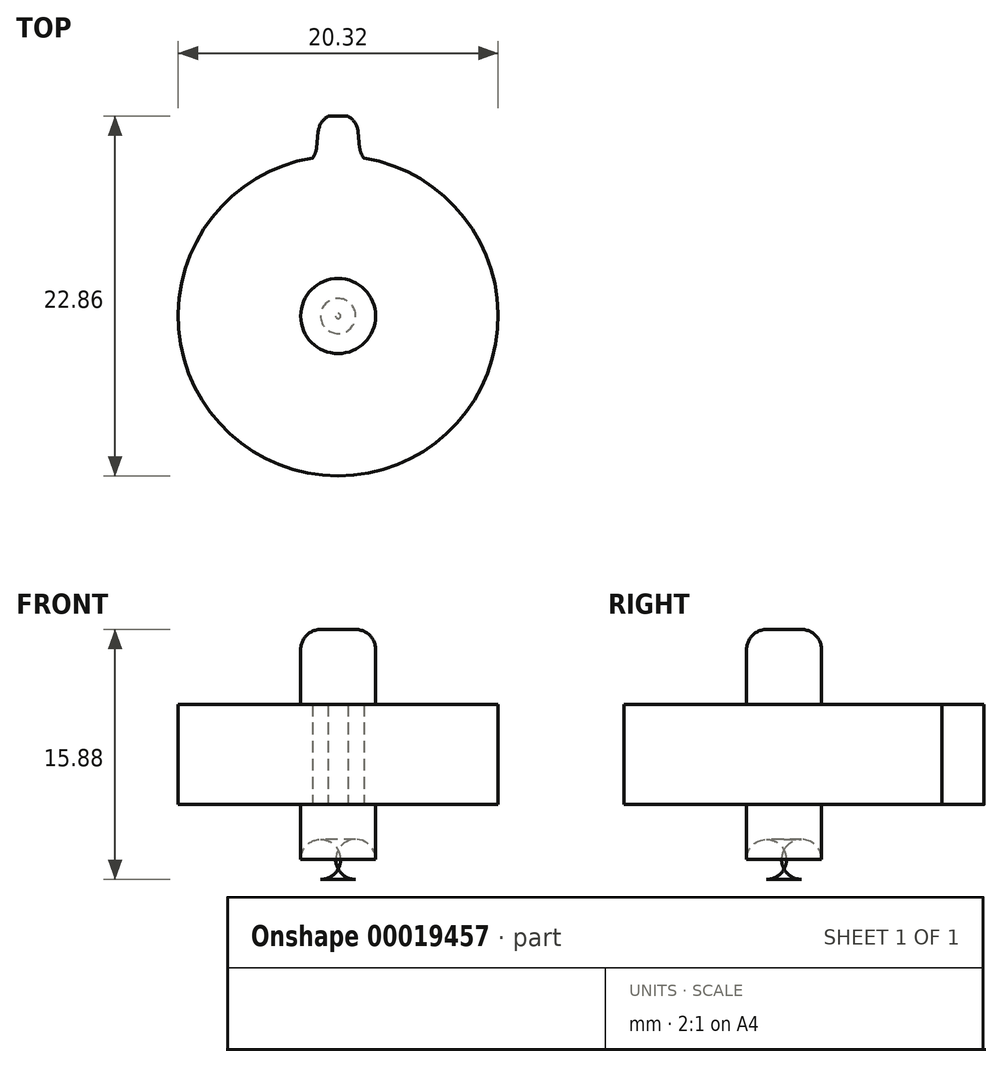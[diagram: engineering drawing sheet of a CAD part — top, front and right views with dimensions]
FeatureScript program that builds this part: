
annotation { "Feature Type Name" : "Feature", "Feature Type Description" : "" }
export const myFeature = defineFeature(function(context is Context, id is Id, definition is map)
    precondition{}
    {
        {
            var Q0;
            Q0=qCreatedBy(makeId("Top.planeOp"),FACE);
            var sketch = newSketch(context, id + "F0", { "sketchPlane" : qUnion([Q0])});
            skArc(sketch, "E0", {"start": v(0.64, 12.68) * mm, "mid": v(0, 12.7) * mm, "end": v(-0.64, 12.68) * mm});
            skLineSegment(sketch, "E1", {"start": v(1.26, 11.72) * mm, "end": v(1.37, 10.68) * mm});
            skCircle(sketch, "E2", {"center": v(0, 0) * mm, "radius": 10.16 * mm});
            skArc(sketch, "E3", {"start": v(1.26, 11.72) * mm, "mid": v(1.07, 12.28) * mm, "end": v(0.64, 12.68) * mm});
            skArc(sketch, "E4", {"start": v(1.37, 10.68) * mm, "mid": v(1.46, 10.33) * mm, "end": v(1.64, 10.03) * mm});
            skLineSegment(sketch, "E5", {"start": v(3.66, 0) * mm, "end": v(0, 0) * mm, "construction": true});
            skLineSegment(sketch, "E6", {"start": v(0, 0) * mm, "end": v(0, 13.54) * mm, "construction": true});
            skLineSegment(sketch, "E7.MirrorCS", {"start": v(-1.26, 11.72) * mm, "end": v(-1.37, 10.68) * mm});
            skArc(sketch, "E8.MirrorCS", {"start": v(-1.26, 11.72) * mm, "mid": v(-1.07, 12.28) * mm, "end": v(-0.64, 12.68) * mm});
            skArc(sketch, "E9.MirrorCS", {"start": v(-1.37, 10.68) * mm, "mid": v(-1.46, 10.33) * mm, "end": v(-1.64, 10.03) * mm});
            skArc(sketch, "E10.1.0", {"start": v(-6.22, 10) * mm, "mid": v(-6.29, 10.6) * mm, "end": v(-6.08, 11.15) * mm});
            skArc(sketch, "E10.1.1", {"start": v(-4.93, 11.7) * mm, "mid": v(-5.51, 11.44) * mm, "end": v(-6.08, 11.15) * mm});
            skArc(sketch, "E10.1.2", {"start": v(-3.95, 11.1) * mm, "mid": v(-4.37, 11.52) * mm, "end": v(-4.93, 11.7) * mm});
            skArc(sketch, "E10.1.3", {"start": v(-5.87, 9.03) * mm, "mid": v(-5.8, 8.68) * mm, "end": v(-5.83, 8.32) * mm});
            skArc(sketch, "E10.1.4", {"start": v(-3.4, 10.22) * mm, "mid": v(-3.17, 9.94) * mm, "end": v(-2.88, 9.74) * mm});
            skLineSegment(sketch, "E10.1.5", {"start": v(-6.22, 10) * mm, "end": v(-5.87, 9.03) * mm});
            skLineSegment(sketch, "E10.1.6", {"start": v(-3.95, 11.1) * mm, "end": v(-3.4, 10.22) * mm});
            skArc(sketch, "E10.2.0", {"start": v(-9.95, 6.32) * mm, "mid": v(-10.26, 6.82) * mm, "end": v(-10.31, 7.41) * mm});
            skArc(sketch, "E10.2.1", {"start": v(-9.52, 8.4) * mm, "mid": v(-9.93, 7.92) * mm, "end": v(-10.31, 7.41) * mm});
            skArc(sketch, "E10.2.2", {"start": v(-8.37, 8.3) * mm, "mid": v(-8.93, 8.49) * mm, "end": v(-9.52, 8.4) * mm});
            skArc(sketch, "E10.2.3", {"start": v(-9.2, 5.59) * mm, "mid": v(-8.99, 5.3) * mm, "end": v(-8.86, 4.97) * mm});
            skArc(sketch, "E10.2.4", {"start": v(-7.5, 7.73) * mm, "mid": v(-7.17, 7.58) * mm, "end": v(-6.82, 7.53) * mm});
            skLineSegment(sketch, "E10.2.5", {"start": v(-9.95, 6.32) * mm, "end": v(-9.2, 5.59) * mm});
            skLineSegment(sketch, "E10.2.6", {"start": v(-8.37, 8.3) * mm, "end": v(-7.5, 7.73) * mm});
            skArc(sketch, "E10.3.0", {"start": v(-11.7, 1.38) * mm, "mid": v(-12.2, 1.7) * mm, "end": v(-12.5, 2.2) * mm});
            skArc(sketch, "E10.3.1", {"start": v(-12.22, 3.44) * mm, "mid": v(-12.38, 2.83) * mm, "end": v(-12.5, 2.2) * mm});
            skArc(sketch, "E10.3.2", {"start": v(-11.14, 3.84) * mm, "mid": v(-11.73, 3.77) * mm, "end": v(-12.22, 3.44) * mm});
            skArc(sketch, "E10.3.3", {"start": v(-10.72, 1.04) * mm, "mid": v(-10.4, 0.88) * mm, "end": v(-10.14, 0.64) * mm});
            skArc(sketch, "E10.3.4", {"start": v(-10.1, 3.71) * mm, "mid": v(-9.75, 3.72) * mm, "end": v(-9.41, 3.83) * mm});
            skLineSegment(sketch, "E10.3.5", {"start": v(-11.7, 1.38) * mm, "end": v(-10.72, 1.04) * mm});
            skLineSegment(sketch, "E10.3.6", {"start": v(-11.14, 3.84) * mm, "end": v(-10.1, 3.71) * mm});
            skArc(sketch, "E10.4.0", {"start": v(-11.14, -3.84) * mm, "mid": v(-11.73, -3.77) * mm, "end": v(-12.22, -3.44) * mm});
            skArc(sketch, "E10.4.1", {"start": v(-12.5, -2.2) * mm, "mid": v(-12.38, -2.83) * mm, "end": v(-12.22, -3.44) * mm});
            skArc(sketch, "E10.4.2", {"start": v(-11.7, -1.38) * mm, "mid": v(-12.2, -1.7) * mm, "end": v(-12.5, -2.2) * mm});
            skArc(sketch, "E10.4.3", {"start": v(-10.1, -3.71) * mm, "mid": v(-9.75, -3.72) * mm, "end": v(-9.41, -3.83) * mm});
            skArc(sketch, "E10.4.4", {"start": v(-10.72, -1.04) * mm, "mid": v(-10.4, -0.88) * mm, "end": v(-10.14, -0.64) * mm});
            skLineSegment(sketch, "E10.4.5", {"start": v(-11.14, -3.84) * mm, "end": v(-10.1, -3.71) * mm});
            skLineSegment(sketch, "E10.4.6", {"start": v(-11.7, -1.38) * mm, "end": v(-10.72, -1.04) * mm});
            skArc(sketch, "E10.5.0", {"start": v(-8.37, -8.3) * mm, "mid": v(-8.93, -8.49) * mm, "end": v(-9.52, -8.4) * mm});
            skArc(sketch, "E10.5.1", {"start": v(-10.31, -7.41) * mm, "mid": v(-9.93, -7.92) * mm, "end": v(-9.52, -8.4) * mm});
            skArc(sketch, "E10.5.2", {"start": v(-9.95, -6.32) * mm, "mid": v(-10.26, -6.82) * mm, "end": v(-10.31, -7.41) * mm});
            skArc(sketch, "E10.5.3", {"start": v(-7.5, -7.73) * mm, "mid": v(-7.17, -7.58) * mm, "end": v(-6.82, -7.53) * mm});
            skArc(sketch, "E10.5.4", {"start": v(-9.2, -5.59) * mm, "mid": v(-8.99, -5.3) * mm, "end": v(-8.86, -4.97) * mm});
            skLineSegment(sketch, "E10.5.5", {"start": v(-8.37, -8.3) * mm, "end": v(-7.5, -7.73) * mm});
            skLineSegment(sketch, "E10.5.6", {"start": v(-9.95, -6.32) * mm, "end": v(-9.2, -5.59) * mm});
            skArc(sketch, "E10.6.0", {"start": v(-3.95, -11.1) * mm, "mid": v(-4.37, -11.52) * mm, "end": v(-4.93, -11.7) * mm});
            skArc(sketch, "E10.6.1", {"start": v(-6.08, -11.15) * mm, "mid": v(-5.51, -11.44) * mm, "end": v(-4.93, -11.7) * mm});
            skArc(sketch, "E10.6.2", {"start": v(-6.22, -10) * mm, "mid": v(-6.29, -10.6) * mm, "end": v(-6.08, -11.15) * mm});
            skArc(sketch, "E10.6.3", {"start": v(-3.4, -10.22) * mm, "mid": v(-3.17, -9.94) * mm, "end": v(-2.88, -9.74) * mm});
            skArc(sketch, "E10.6.4", {"start": v(-5.87, -9.03) * mm, "mid": v(-5.8, -8.68) * mm, "end": v(-5.83, -8.32) * mm});
            skLineSegment(sketch, "E10.6.5", {"start": v(-3.95, -11.1) * mm, "end": v(-3.4, -10.22) * mm});
            skLineSegment(sketch, "E10.6.6", {"start": v(-6.22, -10) * mm, "end": v(-5.87, -9.03) * mm});
            skArc(sketch, "E10.7.0", {"start": v(1.26, -11.72) * mm, "mid": v(1.07, -12.28) * mm, "end": v(0.63, -12.68) * mm});
            skArc(sketch, "E10.7.1", {"start": v(-0.64, -12.68) * mm, "mid": v(0, -12.7) * mm, "end": v(0.64, -12.68) * mm});
            skArc(sketch, "E10.7.2", {"start": v(-1.26, -11.72) * mm, "mid": v(-1.07, -12.28) * mm, "end": v(-0.64, -12.68) * mm});
            skArc(sketch, "E10.7.3", {"start": v(1.37, -10.68) * mm, "mid": v(1.46, -10.33) * mm, "end": v(1.64, -10.03) * mm});
            skArc(sketch, "E10.7.4", {"start": v(-1.37, -10.68) * mm, "mid": v(-1.46, -10.33) * mm, "end": v(-1.64, -10.03) * mm});
            skLineSegment(sketch, "E10.7.5", {"start": v(1.26, -11.72) * mm, "end": v(1.37, -10.68) * mm});
            skLineSegment(sketch, "E10.7.6", {"start": v(-1.26, -11.72) * mm, "end": v(-1.37, -10.68) * mm});
            skArc(sketch, "E10.8.0", {"start": v(6.22, -10) * mm, "mid": v(6.29, -10.6) * mm, "end": v(6.08, -11.15) * mm});
            skArc(sketch, "E10.8.1", {"start": v(4.93, -11.7) * mm, "mid": v(5.51, -11.44) * mm, "end": v(6.08, -11.15) * mm});
            skArc(sketch, "E10.8.2", {"start": v(3.95, -11.1) * mm, "mid": v(4.37, -11.52) * mm, "end": v(4.93, -11.7) * mm});
            skArc(sketch, "E10.8.3", {"start": v(5.87, -9.03) * mm, "mid": v(5.8, -8.68) * mm, "end": v(5.83, -8.32) * mm});
            skArc(sketch, "E10.8.4", {"start": v(3.4, -10.22) * mm, "mid": v(3.17, -9.94) * mm, "end": v(2.88, -9.74) * mm});
            skLineSegment(sketch, "E10.8.5", {"start": v(6.22, -10) * mm, "end": v(5.87, -9.03) * mm});
            skLineSegment(sketch, "E10.8.6", {"start": v(3.95, -11.1) * mm, "end": v(3.4, -10.22) * mm});
            skArc(sketch, "E10.9.0", {"start": v(9.95, -6.32) * mm, "mid": v(10.26, -6.82) * mm, "end": v(10.31, -7.41) * mm});
            skArc(sketch, "E10.9.1", {"start": v(9.52, -8.4) * mm, "mid": v(9.93, -7.92) * mm, "end": v(10.31, -7.41) * mm});
            skArc(sketch, "E10.9.2", {"start": v(8.37, -8.3) * mm, "mid": v(8.93, -8.49) * mm, "end": v(9.52, -8.4) * mm});
            skArc(sketch, "E10.9.3", {"start": v(9.2, -5.59) * mm, "mid": v(8.99, -5.3) * mm, "end": v(8.86, -4.97) * mm});
            skArc(sketch, "E10.9.4", {"start": v(7.5, -7.73) * mm, "mid": v(7.17, -7.58) * mm, "end": v(6.82, -7.53) * mm});
            skLineSegment(sketch, "E10.9.5", {"start": v(9.95, -6.32) * mm, "end": v(9.2, -5.59) * mm});
            skLineSegment(sketch, "E10.9.6", {"start": v(8.37, -8.3) * mm, "end": v(7.5, -7.73) * mm});
            skArc(sketch, "E10.10.0", {"start": v(11.7, -1.38) * mm, "mid": v(12.2, -1.7) * mm, "end": v(12.5, -2.2) * mm});
            skArc(sketch, "E10.10.1", {"start": v(12.22, -3.44) * mm, "mid": v(12.38, -2.83) * mm, "end": v(12.5, -2.2) * mm});
            skArc(sketch, "E10.10.2", {"start": v(11.14, -3.84) * mm, "mid": v(11.73, -3.77) * mm, "end": v(12.22, -3.44) * mm});
            skArc(sketch, "E10.10.3", {"start": v(10.72, -1.04) * mm, "mid": v(10.4, -0.88) * mm, "end": v(10.14, -0.64) * mm});
            skArc(sketch, "E10.10.4", {"start": v(10.1, -3.71) * mm, "mid": v(9.75, -3.72) * mm, "end": v(9.41, -3.83) * mm});
            skLineSegment(sketch, "E10.10.5", {"start": v(11.7, -1.38) * mm, "end": v(10.72, -1.04) * mm});
            skLineSegment(sketch, "E10.10.6", {"start": v(11.14, -3.84) * mm, "end": v(10.1, -3.71) * mm});
            skArc(sketch, "E10.11.0", {"start": v(11.14, 3.84) * mm, "mid": v(11.73, 3.77) * mm, "end": v(12.22, 3.44) * mm});
            skArc(sketch, "E10.11.1", {"start": v(12.5, 2.2) * mm, "mid": v(12.38, 2.83) * mm, "end": v(12.22, 3.44) * mm});
            skArc(sketch, "E10.11.2", {"start": v(11.7, 1.38) * mm, "mid": v(12.2, 1.7) * mm, "end": v(12.5, 2.2) * mm});
            skArc(sketch, "E10.11.3", {"start": v(10.1, 3.71) * mm, "mid": v(9.75, 3.72) * mm, "end": v(9.41, 3.83) * mm});
            skArc(sketch, "E10.11.4", {"start": v(10.72, 1.04) * mm, "mid": v(10.4, 0.88) * mm, "end": v(10.14, 0.63) * mm});
            skLineSegment(sketch, "E10.11.5", {"start": v(11.14, 3.84) * mm, "end": v(10.1, 3.71) * mm});
            skLineSegment(sketch, "E10.11.6", {"start": v(11.7, 1.38) * mm, "end": v(10.72, 1.04) * mm});
            skCircle(sketch, "E11", {"center": v(0, 0) * mm, "radius": 2.38 * mm});
            skArc(sketch, "E12.2.12.0", {"start": v(8.37, 8.3) * mm, "mid": v(8.93, 8.49) * mm, "end": v(9.52, 8.4) * mm});
            skArc(sketch, "E12.4.12.0", {"start": v(10.31, 7.41) * mm, "mid": v(9.93, 7.92) * mm, "end": v(9.52, 8.4) * mm});
            skArc(sketch, "E12.8.12.0", {"start": v(9.95, 6.32) * mm, "mid": v(10.26, 6.82) * mm, "end": v(10.31, 7.41) * mm});
            skArc(sketch, "E12.12.12.0", {"start": v(7.5, 7.73) * mm, "mid": v(7.17, 7.58) * mm, "end": v(6.82, 7.53) * mm});
            skArc(sketch, "E12.16.12.0", {"start": v(9.2, 5.59) * mm, "mid": v(8.99, 5.3) * mm, "end": v(8.86, 4.97) * mm});
            skLineSegment(sketch, "E12.20.12.0", {"start": v(8.37, 8.3) * mm, "end": v(7.5, 7.73) * mm});
            skLineSegment(sketch, "E12.23.12.0", {"start": v(9.95, 6.32) * mm, "end": v(9.2, 5.59) * mm});
            skArc(sketch, "E12.2.13.0", {"start": v(3.95, 11.1) * mm, "mid": v(4.37, 11.52) * mm, "end": v(4.93, 11.7) * mm});
            skArc(sketch, "E12.4.13.0", {"start": v(6.08, 11.15) * mm, "mid": v(5.51, 11.44) * mm, "end": v(4.93, 11.7) * mm});
            skArc(sketch, "E12.8.13.0", {"start": v(6.22, 10) * mm, "mid": v(6.29, 10.6) * mm, "end": v(6.08, 11.15) * mm});
            skArc(sketch, "E12.12.13.0", {"start": v(3.4, 10.22) * mm, "mid": v(3.17, 9.94) * mm, "end": v(2.88, 9.74) * mm});
            skArc(sketch, "E12.16.13.0", {"start": v(5.87, 9.03) * mm, "mid": v(5.8, 8.68) * mm, "end": v(5.83, 8.32) * mm});
            skLineSegment(sketch, "E12.20.13.0", {"start": v(3.95, 11.1) * mm, "end": v(3.4, 10.22) * mm});
            skLineSegment(sketch, "E12.23.13.0", {"start": v(6.22, 10) * mm, "end": v(5.87, 9.03) * mm});
            skSolve(sketch);
        }
        {
            var Q0;
            Q0=makeQuery(id+"F0.imprint","IMPRINT",FACE,{"disambiguationData":[TD([[makeQuery(id+"F0.imprint","IMPRINT",EDGE,{"derivedFrom":sQuery(id+"F0.wireOp",EDGE,"E11")}),-1.0]])]});
            var Q1;
            Q1=makeQuery(id+"F0.imprint","IMPRINT",FACE,{"disambiguationData":[TD([[makeQuery(id+"F0.imprint","IMPRINT",EDGE,{"derivedFrom":sQuery(id+"F0.wireOp",EDGE,"E10.2.0")}),-1.0]])]});
            var Q2;
            Q2=makeQuery(id+"F0.imprint","IMPRINT",FACE,{"disambiguationData":[TD([[makeQuery(id+"F0.imprint","IMPRINT",EDGE,{"derivedFrom":sQuery(id+"F0.wireOp",EDGE,"E10.1.0")}),-1.0]])]});
            var Q3;
            Q3=makeQuery(id+"F0.imprint","IMPRINT",FACE,{"disambiguationData":[TD([[makeQuery(id+"F0.imprint","IMPRINT",EDGE,{"derivedFrom":sQuery(id+"F0.wireOp",EDGE,"E0")}),1.0]])]});
            var Q4;
            Q4=makeQuery(id+"F0.imprint","IMPRINT",FACE,{"disambiguationData":[TD([[makeQuery(id+"F0.imprint","IMPRINT",EDGE,{"derivedFrom":sQuery(id+"F0.wireOp",EDGE,"E12.2.13.0")}),-1.0]])]});
            var Q5;
            Q5=makeQuery(id+"F0.imprint","IMPRINT",FACE,{"disambiguationData":[TD([[makeQuery(id+"F0.imprint","IMPRINT",EDGE,{"derivedFrom":sQuery(id+"F0.wireOp",EDGE,"E12.2.12.0")}),-1.0]])]});
            var Q6;
            Q6=makeQuery(id+"F0.imprint","IMPRINT",FACE,{"disambiguationData":[TD([[makeQuery(id+"F0.imprint","IMPRINT",EDGE,{"derivedFrom":sQuery(id+"F0.wireOp",EDGE,"E10.11.0")}),-1.0]])]});
            var Q7;
            Q7=makeQuery(id+"F0.imprint","IMPRINT",FACE,{"disambiguationData":[TD([[makeQuery(id+"F0.imprint","IMPRINT",EDGE,{"derivedFrom":sQuery(id+"F0.wireOp",EDGE,"E10.10.0")}),-1.0]])]});
            var Q8;
            Q8=makeQuery(id+"F0.imprint","IMPRINT",FACE,{"disambiguationData":[TD([[makeQuery(id+"F0.imprint","IMPRINT",EDGE,{"derivedFrom":sQuery(id+"F0.wireOp",EDGE,"E10.3.0")}),-1.0]])]});
            var Q9;
            Q9=makeQuery(id+"F0.imprint","IMPRINT",FACE,{"disambiguationData":[TD([[makeQuery(id+"F0.imprint","IMPRINT",EDGE,{"derivedFrom":sQuery(id+"F0.wireOp",EDGE,"E10.4.0")}),-1.0]])]});
            var Q10;
            Q10=makeQuery(id+"F0.imprint","IMPRINT",FACE,{"disambiguationData":[TD([[makeQuery(id+"F0.imprint","IMPRINT",EDGE,{"derivedFrom":sQuery(id+"F0.wireOp",EDGE,"E10.5.0")}),-1.0]])]});
            var Q11;
            Q11=makeQuery(id+"F0.imprint","IMPRINT",FACE,{"disambiguationData":[TD([[makeQuery(id+"F0.imprint","IMPRINT",EDGE,{"derivedFrom":sQuery(id+"F0.wireOp",EDGE,"E10.6.0")}),-1.0]])]});
            var Q12;
            Q12=makeQuery(id+"F0.imprint","IMPRINT",FACE,{"disambiguationData":[TD([[makeQuery(id+"F0.imprint","IMPRINT",EDGE,{"derivedFrom":sQuery(id+"F0.wireOp",EDGE,"E10.7.0")}),-1.0]])]});
            extrude(context, id + "F1", {"entities" : qUnion([Q0, Q1, Q2, Q3, Q4, Q5, Q6, Q7, Q8, Q9, Q10, Q11, Q12]), "endBound" : BoundingType.SYMMETRIC, "depth" : 6.35 * mm});
        }
        {
            var Q0;
            Q0=makeQuery(id+"F0.imprint","IMPRINT",FACE,{"disambiguationData":[TD([[makeQuery(id+"F0.imprint","IMPRINT",EDGE,{"derivedFrom":sQuery(id+"F0.wireOp",EDGE,"E11")}),1.0]])]});
            extrude(context, id + "F2", {"entities" : qUnion([Q0]), "operationType" : NewBodyOperationType.ADD, "endBound" : BoundingType.SYMMETRIC, "depth" : 15.88 * mm});
        }
        {
            var Q0;
            Q0=makeQuery(id+"F2.opExtrude","CAP_EDGE",EDGE,{"disambiguationData":[OSD([sQuery(id+"F0.wireOp",EDGE,"E11")])],"isStart":false});
            var Q1;
            Q1=makeQuery(id+"F2.opExtrude","CAP_EDGE",EDGE,{"disambiguationData":[OSD([sQuery(id+"F0.wireOp",EDGE,"E11")])],"isStart":true});
            fillet(context, id + "F3", {"entities" : qUnion([Q0, Q1]), "radius" : 1.27 * mm, "tangentPropagation" : true, "allowEdgeOverflow" : false});
        }
    });
